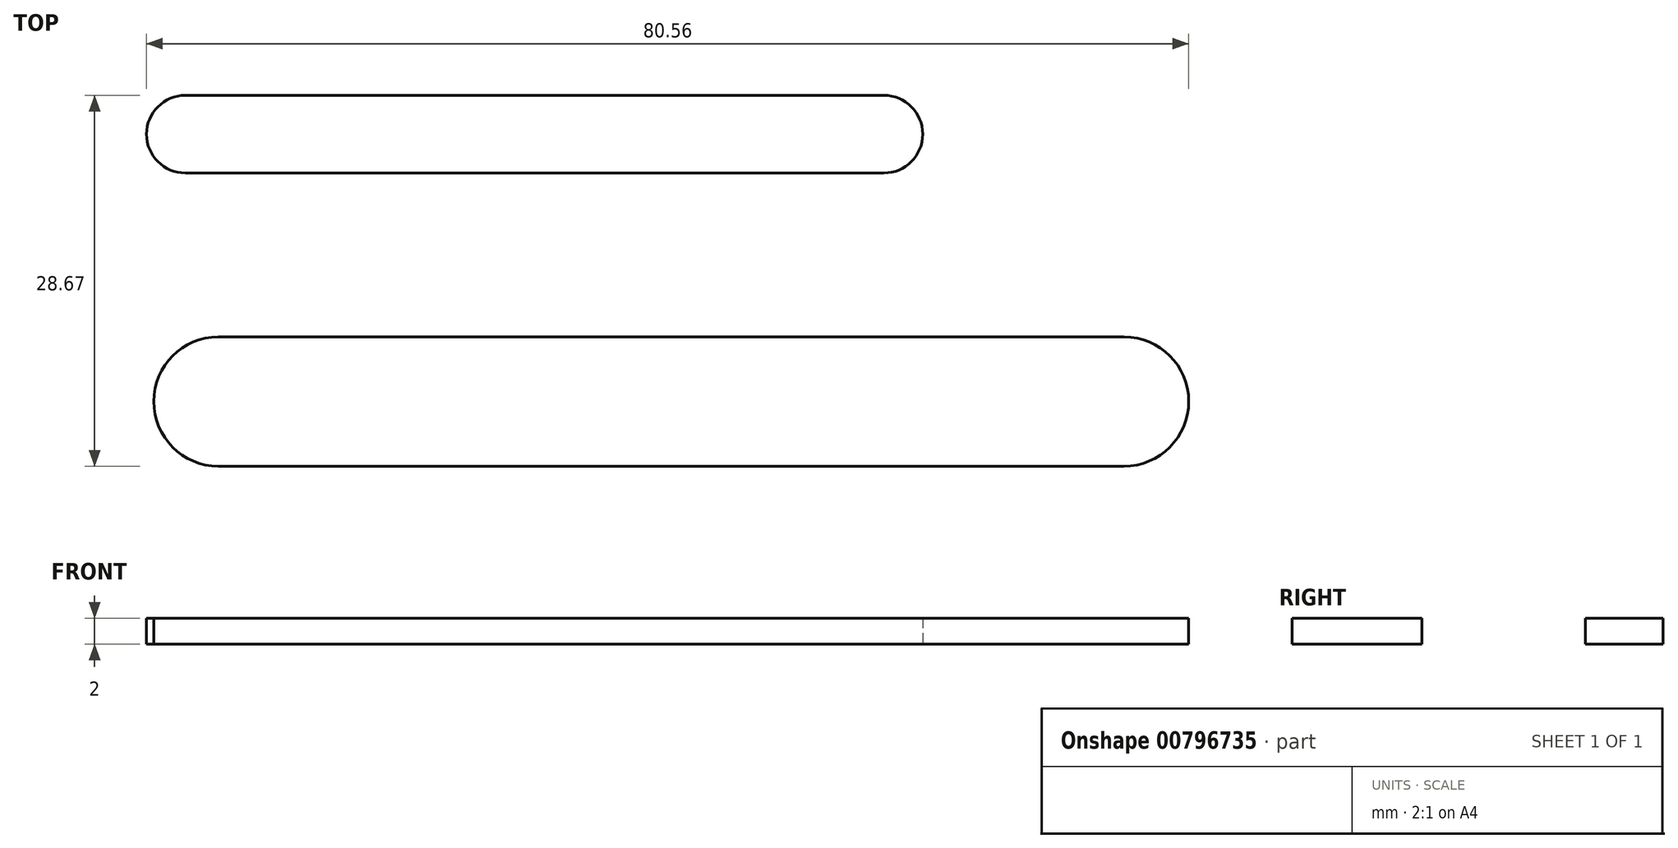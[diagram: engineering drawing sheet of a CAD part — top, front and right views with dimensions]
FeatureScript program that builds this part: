
annotation { "Feature Type Name" : "Feature", "Feature Type Description" : "" }
export const myFeature = defineFeature(function(context is Context, id is Id, definition is map)
    precondition{}
    {
        {
            var Q0;
            Q0=qCreatedBy(makeId("Top.planeOp"),FACE);
            var sketch = newSketch(context, id + "F0", { "sketchPlane" : qUnion([Q0])});
            skArc(sketch, "E0", {"start": v(-32.32, 8.33) * mm, "mid": v(-35.32, 5.33) * mm, "end": v(-32.32, 2.33) * mm});
            skArc(sketch, "E1", {"start": v(21.68, 2.33) * mm, "mid": v(24.68, 5.33) * mm, "end": v(21.68, 8.33) * mm});
            skLineSegment(sketch, "E2", {"start": v(-32.32, 8.33) * mm, "end": v(21.68, 8.33) * mm});
            skLineSegment(sketch, "E3", {"start": v(-32.32, 2.33) * mm, "end": v(21.68, 2.33) * mm});
            skArc(sketch, "E4", {"start": v(-29.76, -10.34) * mm, "mid": v(-34.76, -15.34) * mm, "end": v(-29.76, -20.34) * mm});
            skArc(sketch, "E5", {"start": v(40.24, -20.34) * mm, "mid": v(45.24, -15.34) * mm, "end": v(40.24, -10.34) * mm});
            skLineSegment(sketch, "E6", {"start": v(-29.76, -10.34) * mm, "end": v(40.24, -10.34) * mm});
            skLineSegment(sketch, "E7", {"start": v(-29.76, -20.34) * mm, "end": v(40.24, -20.34) * mm});
            skSolve(sketch);
        }
        {
            var Q0;
            Q0=makeQuery(id+"F0.imprint","IMPRINT",FACE,{"disambiguationData":[TD([[makeQuery(id+"F0.imprint","IMPRINT",EDGE,{"derivedFrom":sQuery(id+"F0.wireOp",EDGE,"E0")}),1.0]])]});
            extrude(context, id + "F1", {"entities" : qUnion([Q0]), "depth" : 2 * mm, "offsetDistance" : 25 * mm});
        }
        {
            var Q0;
            Q0=makeQuery(id+"F0.imprint","IMPRINT",FACE,{"disambiguationData":[TD([[makeQuery(id+"F0.imprint","IMPRINT",EDGE,{"derivedFrom":sQuery(id+"F0.wireOp",EDGE,"E4")}),1.0]])]});
            extrude(context, id + "F2", {"entities" : qUnion([Q0]), "depth" : 2 * mm, "offsetDistance" : 25 * mm});
        }
    });
